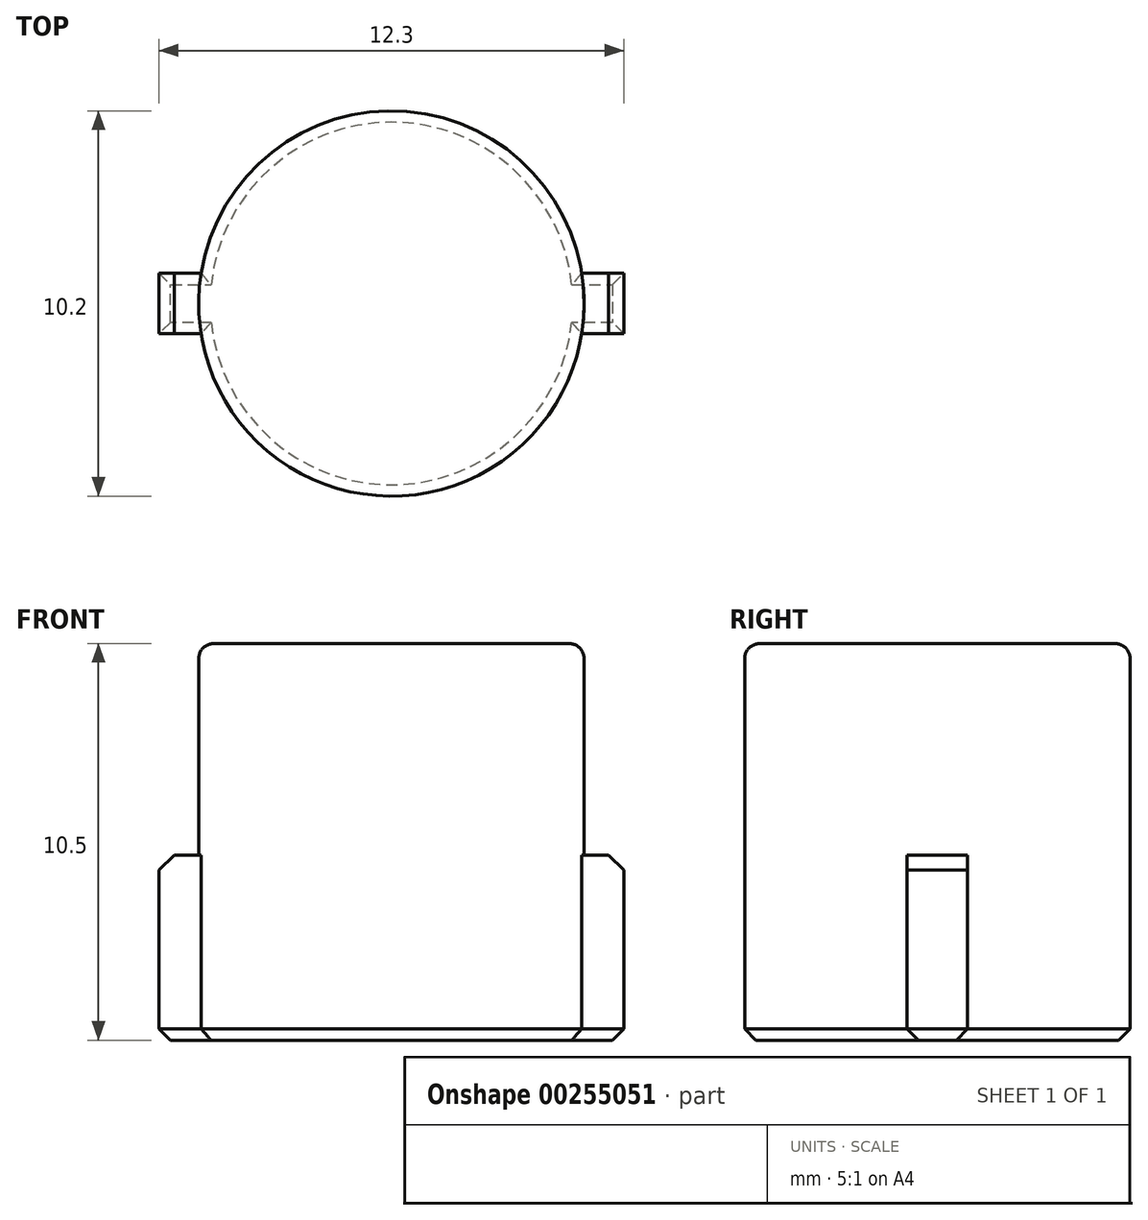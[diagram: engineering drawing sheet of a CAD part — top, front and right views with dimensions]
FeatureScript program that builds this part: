
annotation { "Feature Type Name" : "Feature", "Feature Type Description" : "" }
export const myFeature = defineFeature(function(context is Context, id is Id, definition is map)
    precondition{}
    {
        {
            var Q0;
            Q0=qCreatedBy(makeId("Top.planeOp"),FACE);
            var sketch = newSketch(context, id + "F0", { "sketchPlane" : qUnion([Q0])});
            skCircle(sketch, "E0", {"center": v(0, 0) * mm, "radius": 5.1 * mm});
            skSolve(sketch);
        }
        {
            var Q0;
            Q0=qSketchRegion(id+"F0",true);
            extrude(context, id + "F1", {"entities" : qUnion([Q0]), "depth" : 12.8 * mm});
        }
        {
            var Q0;
            Q0=makeQuery(id+"F1.opExtrude","CAP_FACE",FACE,{"disambiguationData":[OSD([sQuery(id+"F0.wireOp",EDGE,"E0")])],"isStart":true});
            var sketch = newSketch(context, id + "F2", { "sketchPlane" : qUnion([Q0])});
            skLineSegment(sketch, "E1.bottom", {"start": v(6.15, 0.8) * mm, "end": v(-6.15, 0.8) * mm});
            skLineSegment(sketch, "E1.top", {"start": v(6.15, -0.8) * mm, "end": v(-6.15, -0.8) * mm});
            skLineSegment(sketch, "E1.left", {"start": v(6.15, 0.8) * mm, "end": v(6.15, -0.8) * mm});
            skLineSegment(sketch, "E1.right", {"start": v(-6.15, 0.8) * mm, "end": v(-6.15, -0.8) * mm});
            skPoint(sketch, "E1.middle", {"position": v(0, 0) * mm});
            skCircle(sketch, "E2", {"center": v(0, 0) * mm, "radius": 6.2 * mm});
            skLineSegment(sketch, "E3.1.0", {"start": v(5.72, 2.38) * mm, "end": v(-4.92, -3.77) * mm});
            skLineSegment(sketch, "E3.1.1", {"start": v(4.92, 3.77) * mm, "end": v(-5.72, -2.38) * mm});
            skLineSegment(sketch, "E3.2.0", {"start": v(3.77, 4.92) * mm, "end": v(-2.38, -5.72) * mm});
            skLineSegment(sketch, "E3.2.1", {"start": v(2.38, 5.72) * mm, "end": v(-3.77, -4.92) * mm});
            skLineSegment(sketch, "E3.3.0", {"start": v(0.8, 6.15) * mm, "end": v(0.8, -6.15) * mm});
            skLineSegment(sketch, "E3.3.1", {"start": v(-0.8, 6.15) * mm, "end": v(-0.8, -6.15) * mm});
            skLineSegment(sketch, "E3.4.0", {"start": v(-2.38, 5.72) * mm, "end": v(3.77, -4.92) * mm});
            skLineSegment(sketch, "E3.4.1", {"start": v(-3.77, 4.92) * mm, "end": v(2.38, -5.72) * mm});
            skLineSegment(sketch, "E3.5.0", {"start": v(-4.92, 3.77) * mm, "end": v(5.72, -2.38) * mm});
            skLineSegment(sketch, "E3.5.1", {"start": v(-5.72, 2.38) * mm, "end": v(4.92, -3.77) * mm});
            skLineSegment(sketch, "E3.6.0", {"start": v(-6.15, 0.8) * mm, "end": v(6.15, 0.8) * mm});
            skLineSegment(sketch, "E3.6.1", {"start": v(-6.15, -0.8) * mm, "end": v(6.15, -0.8) * mm});
            skLineSegment(sketch, "E3.7.0", {"start": v(-5.72, -2.38) * mm, "end": v(4.92, 3.77) * mm});
            skLineSegment(sketch, "E3.7.1", {"start": v(-4.92, -3.77) * mm, "end": v(5.72, 2.38) * mm});
            skLineSegment(sketch, "E3.8.0", {"start": v(-3.77, -4.92) * mm, "end": v(2.38, 5.72) * mm});
            skLineSegment(sketch, "E3.8.1", {"start": v(-2.38, -5.72) * mm, "end": v(3.77, 4.92) * mm});
            skLineSegment(sketch, "E3.9.0", {"start": v(-0.8, -6.15) * mm, "end": v(-0.8, 6.15) * mm});
            skLineSegment(sketch, "E3.9.1", {"start": v(0.8, -6.15) * mm, "end": v(0.8, 6.15) * mm});
            skLineSegment(sketch, "E3.10.0", {"start": v(2.38, -5.72) * mm, "end": v(-3.77, 4.92) * mm});
            skLineSegment(sketch, "E3.10.1", {"start": v(3.77, -4.92) * mm, "end": v(-2.38, 5.72) * mm});
            skLineSegment(sketch, "E3.11.0", {"start": v(4.92, -3.77) * mm, "end": v(-5.72, 2.38) * mm});
            skLineSegment(sketch, "E3.11.1", {"start": v(5.72, -2.38) * mm, "end": v(-4.92, 3.77) * mm});
            skSolve(sketch);
        }
        {
            var Q0;
            {var subQ0=sQuery(id+"F2.wireOp",EDGE,"E3.8.0");var subQ1=sQuery(id+"F2.wireOp",EDGE,"E2");var subQ2=makeQuery(id+"F2.imprint","INTERSECT",VERTEX,{"disambiguationData":[OD(1.0)],"derivedFrom":[subQ1,subQ0]});Q0=makeQuery(id+"F2.imprint","IMPRINT",FACE,{"disambiguationData":[TD([[makeQuery(id+"F2.imprint","IMPRINT",EDGE,{"disambiguationData":[TD([[subQ2,1.0]])],"derivedFrom":subQ1}),1.0]])]});}
            var Q1;
            {var subQ0=sQuery(id+"F2.wireOp",EDGE,"E3.7.0");var subQ1=sQuery(id+"F2.wireOp",EDGE,"E2");var subQ2=makeQuery(id+"F2.imprint","INTERSECT",VERTEX,{"disambiguationData":[OD(1.0)],"derivedFrom":[subQ1,subQ0]});Q1=makeQuery(id+"F2.imprint","IMPRINT",FACE,{"disambiguationData":[TD([[makeQuery(id+"F2.imprint","IMPRINT",EDGE,{"disambiguationData":[TD([[subQ2,1.0]])],"derivedFrom":subQ1}),1.0]])]});}
            var Q2;
            {var subQ0=sQuery(id+"F2.wireOp",EDGE,"E1.left");Q2=makeQuery(id+"F2.imprint","IMPRINT",FACE,{"disambiguationData":[TD([[makeQuery(id+"F2.imprint","IMPRINT",EDGE,{"derivedFrom":subQ0}),-1.0]])]});}
            var Q3;
            {var subQ0=sQuery(id+"F2.wireOp",EDGE,"E3.11.0");var subQ1=sQuery(id+"F2.wireOp",EDGE,"E2");var subQ2=makeQuery(id+"F2.imprint","INTERSECT",VERTEX,{"disambiguationData":[OD(0.0)],"derivedFrom":[subQ1,subQ0]});Q3=makeQuery(id+"F2.imprint","IMPRINT",FACE,{"disambiguationData":[TD([[makeQuery(id+"F2.imprint","IMPRINT",EDGE,{"disambiguationData":[TD([[subQ2,-1.0]])],"derivedFrom":subQ1}),1.0]])]});}
            var Q4;
            {var subQ0=sQuery(id+"F2.wireOp",EDGE,"E3.10.0");var subQ1=sQuery(id+"F2.wireOp",EDGE,"E2");var subQ2=makeQuery(id+"F2.imprint","INTERSECT",VERTEX,{"disambiguationData":[OD(0.0)],"derivedFrom":[subQ1,subQ0]});Q4=makeQuery(id+"F2.imprint","IMPRINT",FACE,{"disambiguationData":[TD([[makeQuery(id+"F2.imprint","IMPRINT",EDGE,{"disambiguationData":[TD([[subQ2,-1.0]])],"derivedFrom":subQ1}),1.0]])]});}
            var Q5;
            {var subQ0=sQuery(id+"F2.wireOp",EDGE,"E3.8.0");var subQ1=sQuery(id+"F2.wireOp",EDGE,"E2");var subQ2=makeQuery(id+"F2.imprint","INTERSECT",VERTEX,{"disambiguationData":[OD(0.0)],"derivedFrom":[subQ1,subQ0]});Q5=makeQuery(id+"F2.imprint","IMPRINT",FACE,{"disambiguationData":[TD([[makeQuery(id+"F2.imprint","IMPRINT",EDGE,{"disambiguationData":[TD([[subQ2,-1.0]])],"derivedFrom":subQ1}),1.0]])]});}
            var Q6;
            {var subQ0=sQuery(id+"F2.wireOp",EDGE,"E3.9.0");var subQ1=sQuery(id+"F2.wireOp",EDGE,"E2");var subQ2=makeQuery(id+"F2.imprint","INTERSECT",VERTEX,{"disambiguationData":[OD(0.0)],"derivedFrom":[subQ1,subQ0]});Q6=makeQuery(id+"F2.imprint","IMPRINT",FACE,{"disambiguationData":[TD([[makeQuery(id+"F2.imprint","IMPRINT",EDGE,{"disambiguationData":[TD([[subQ2,-1.0]])],"derivedFrom":subQ1}),1.0]])]});}
            var Q7;
            {var subQ0=sQuery(id+"F2.wireOp",EDGE,"E3.7.0");var subQ1=sQuery(id+"F2.wireOp",EDGE,"E2");var subQ2=makeQuery(id+"F2.imprint","INTERSECT",VERTEX,{"disambiguationData":[OD(0.0)],"derivedFrom":[subQ1,subQ0]});Q7=makeQuery(id+"F2.imprint","IMPRINT",FACE,{"disambiguationData":[TD([[makeQuery(id+"F2.imprint","IMPRINT",EDGE,{"disambiguationData":[TD([[subQ2,-1.0]])],"derivedFrom":subQ1}),1.0]])]});}
            var Q8;
            {var subQ0=sQuery(id+"F2.wireOp",EDGE,"E1.right");Q8=makeQuery(id+"F2.imprint","IMPRINT",FACE,{"disambiguationData":[TD([[makeQuery(id+"F2.imprint","IMPRINT",EDGE,{"derivedFrom":subQ0}),1.0]])]});}
            var Q9;
            {var subQ0=sQuery(id+"F2.wireOp",EDGE,"E3.11.0");var subQ1=sQuery(id+"F2.wireOp",EDGE,"E2");var subQ2=makeQuery(id+"F2.imprint","INTERSECT",VERTEX,{"disambiguationData":[OD(1.0)],"derivedFrom":[subQ1,subQ0]});Q9=makeQuery(id+"F2.imprint","IMPRINT",FACE,{"disambiguationData":[TD([[makeQuery(id+"F2.imprint","IMPRINT",EDGE,{"disambiguationData":[TD([[subQ2,1.0]])],"derivedFrom":subQ1}),1.0]])]});}
            var Q10;
            {var subQ0=sQuery(id+"F2.wireOp",EDGE,"E3.10.0");var subQ1=sQuery(id+"F2.wireOp",EDGE,"E2");var subQ2=makeQuery(id+"F2.imprint","INTERSECT",VERTEX,{"disambiguationData":[OD(1.0)],"derivedFrom":[subQ1,subQ0]});Q10=makeQuery(id+"F2.imprint","IMPRINT",FACE,{"disambiguationData":[TD([[makeQuery(id+"F2.imprint","IMPRINT",EDGE,{"disambiguationData":[TD([[subQ2,1.0]])],"derivedFrom":subQ1}),1.0]])]});}
            var Q11;
            {var subQ0=sQuery(id+"F2.wireOp",EDGE,"E3.9.0");var subQ1=sQuery(id+"F2.wireOp",EDGE,"E2");var subQ2=makeQuery(id+"F2.imprint","INTERSECT",VERTEX,{"disambiguationData":[OD(1.0)],"derivedFrom":[subQ1,subQ0]});Q11=makeQuery(id+"F2.imprint","IMPRINT",FACE,{"disambiguationData":[TD([[makeQuery(id+"F2.imprint","IMPRINT",EDGE,{"disambiguationData":[TD([[subQ2,1.0]])],"derivedFrom":subQ1}),1.0]])]});}
            extrude(context, id + "F3", {"entities" : qUnion([Q0, Q1, Q2, Q3, Q4, Q5, Q6, Q7, Q8, Q9, Q10, Q11]), "operationType" : NewBodyOperationType.ADD, "oppositeDirection" : true, "depth" : 7.2 * mm});
        }
        {
            var Q0;
            {var subQ0=sQuery(id+"F2.wireOp",EDGE,"E2");Q0=makeQuery(id+"F3.opExtrude","CAP_EDGE",EDGE,{"disambiguationData":[OSD([subQ0]),TDD([makeQuery(id+"F2.imprint","IMPRINT",EDGE,{"disambiguationData":[TD([[makeQuery(id+"F2.imprint","INTERSECT",VERTEX,{"disambiguationData":[OD(1.0)],"derivedFrom":[subQ0,sQuery(id+"F2.wireOp",EDGE,"E3.9.0")]}),1.0]])],"derivedFrom":subQ0})])],"isStart":false});}
            var Q1;
            {var subQ0=sQuery(id+"F2.wireOp",EDGE,"E2");Q1=makeQuery(id+"F3.opExtrude","CAP_EDGE",EDGE,{"disambiguationData":[OSD([subQ0]),TDD([makeQuery(id+"F2.imprint","IMPRINT",EDGE,{"disambiguationData":[TD([[makeQuery(id+"F2.imprint","INTERSECT",VERTEX,{"disambiguationData":[OD(1.0)],"derivedFrom":[subQ0,sQuery(id+"F2.wireOp",EDGE,"E3.10.0")]}),1.0]])],"derivedFrom":subQ0})])],"isStart":false});}
            var Q2;
            {var subQ0=sQuery(id+"F2.wireOp",EDGE,"E2");Q2=makeQuery(id+"F3.opExtrude","CAP_EDGE",EDGE,{"disambiguationData":[OSD([subQ0]),TDD([makeQuery(id+"F2.imprint","IMPRINT",EDGE,{"disambiguationData":[TD([[makeQuery(id+"F2.imprint","INTERSECT",VERTEX,{"disambiguationData":[OD(1.0)],"derivedFrom":[subQ0,sQuery(id+"F2.wireOp",EDGE,"E3.11.0")]}),1.0]])],"derivedFrom":subQ0})])],"isStart":false});}
            var Q3;
            Q3=makeQuery(id+"F3.opExtrude","CAP_EDGE",EDGE,{"disambiguationData":[OSD([sQuery(id+"F2.wireOp",EDGE,"E1.right")])],"isStart":false});
            var Q4;
            {var subQ0=sQuery(id+"F2.wireOp",EDGE,"E2");Q4=makeQuery(id+"F3.opExtrude","CAP_EDGE",EDGE,{"disambiguationData":[OSD([subQ0]),TDD([makeQuery(id+"F2.imprint","IMPRINT",EDGE,{"disambiguationData":[TD([[makeQuery(id+"F2.imprint","INTERSECT",VERTEX,{"disambiguationData":[OD(1.0)],"derivedFrom":[subQ0,sQuery(id+"F2.wireOp",EDGE,"E3.8.0")]}),1.0]])],"derivedFrom":subQ0})])],"isStart":false});}
            var Q5;
            {var subQ0=sQuery(id+"F2.wireOp",EDGE,"E2");Q5=makeQuery(id+"F3.opExtrude","CAP_EDGE",EDGE,{"disambiguationData":[OSD([subQ0]),TDD([makeQuery(id+"F2.imprint","IMPRINT",EDGE,{"disambiguationData":[TD([[makeQuery(id+"F2.imprint","INTERSECT",VERTEX,{"disambiguationData":[OD(1.0)],"derivedFrom":[subQ0,sQuery(id+"F2.wireOp",EDGE,"E3.7.0")]}),1.0]])],"derivedFrom":subQ0})])],"isStart":false});}
            var Q6;
            Q6=makeQuery(id+"F3.opExtrude","CAP_EDGE",EDGE,{"disambiguationData":[OSD([sQuery(id+"F2.wireOp",EDGE,"E1.left")])],"isStart":false});
            var Q7;
            {var subQ0=sQuery(id+"F2.wireOp",EDGE,"E2");Q7=makeQuery(id+"F3.opExtrude","CAP_EDGE",EDGE,{"disambiguationData":[OSD([subQ0]),TDD([makeQuery(id+"F2.imprint","IMPRINT",EDGE,{"disambiguationData":[TD([[makeQuery(id+"F2.imprint","INTERSECT",VERTEX,{"disambiguationData":[OD(0.0)],"derivedFrom":[subQ0,sQuery(id+"F2.wireOp",EDGE,"E3.11.0")]}),-1.0]])],"derivedFrom":subQ0})])],"isStart":false});}
            var Q8;
            {var subQ0=sQuery(id+"F2.wireOp",EDGE,"E2");Q8=makeQuery(id+"F3.opExtrude","CAP_EDGE",EDGE,{"disambiguationData":[OSD([subQ0]),TDD([makeQuery(id+"F2.imprint","IMPRINT",EDGE,{"disambiguationData":[TD([[makeQuery(id+"F2.imprint","INTERSECT",VERTEX,{"disambiguationData":[OD(0.0)],"derivedFrom":[subQ0,sQuery(id+"F2.wireOp",EDGE,"E3.10.0")]}),-1.0]])],"derivedFrom":subQ0})])],"isStart":false});}
            var Q9;
            {var subQ0=sQuery(id+"F2.wireOp",EDGE,"E2");Q9=makeQuery(id+"F3.opExtrude","CAP_EDGE",EDGE,{"disambiguationData":[OSD([subQ0]),TDD([makeQuery(id+"F2.imprint","IMPRINT",EDGE,{"disambiguationData":[TD([[makeQuery(id+"F2.imprint","INTERSECT",VERTEX,{"disambiguationData":[OD(0.0)],"derivedFrom":[subQ0,sQuery(id+"F2.wireOp",EDGE,"E3.9.0")]}),-1.0]])],"derivedFrom":subQ0})])],"isStart":false});}
            var Q10;
            {var subQ0=sQuery(id+"F2.wireOp",EDGE,"E2");Q10=makeQuery(id+"F3.opExtrude","CAP_EDGE",EDGE,{"disambiguationData":[OSD([subQ0]),TDD([makeQuery(id+"F2.imprint","IMPRINT",EDGE,{"disambiguationData":[TD([[makeQuery(id+"F2.imprint","INTERSECT",VERTEX,{"disambiguationData":[OD(0.0)],"derivedFrom":[subQ0,sQuery(id+"F2.wireOp",EDGE,"E3.8.0")]}),-1.0]])],"derivedFrom":subQ0})])],"isStart":false});}
            var Q11;
            {var subQ0=sQuery(id+"F2.wireOp",EDGE,"E2");Q11=makeQuery(id+"F3.opExtrude","CAP_EDGE",EDGE,{"disambiguationData":[OSD([subQ0]),TDD([makeQuery(id+"F2.imprint","IMPRINT",EDGE,{"disambiguationData":[TD([[makeQuery(id+"F2.imprint","INTERSECT",VERTEX,{"disambiguationData":[OD(0.0)],"derivedFrom":[subQ0,sQuery(id+"F2.wireOp",EDGE,"E3.7.0")]}),-1.0]])],"derivedFrom":subQ0})])],"isStart":false});}
            chamfer(context, id + "F4", {"entities" : qUnion([Q0, Q1, Q2, Q3, Q4, Q5, Q6, Q7, Q8, Q9, Q10, Q11]), "width" : 0.4 * mm, "tangentPropagation" : true});
        }
        {
            var Q0;
            {var subQ0=sQuery(id+"F2.wireOp",EDGE,"E3.11.0");var subQ1=sQuery(id+"F0.wireOp",EDGE,"E0");var subQ2=makeQuery(id+"F1.opExtrude","CAP_EDGE",EDGE,{"disambiguationData":[OSD([subQ1])],"isStart":true});var subQ3=makeQuery(id+"F2.imprint","INTERSECT",VERTEX,{"disambiguationData":[OD(0.0)],"derivedFrom":[subQ2,subQ0]});var subQ4=sQuery(id+"F2.wireOp",EDGE,"E3.11.1");var subQ6=sQuery(id+"F2.wireOp",EDGE,"E2");var subQ7=makeQuery(id+"F2.imprint","INTERSECT",VERTEX,{"disambiguationData":[OD(0.0)],"derivedFrom":[subQ6,subQ4]});var subQ8=makeQuery(id+"F2.imprint","INTERSECT",VERTEX,{"disambiguationData":[OD(0.0)],"derivedFrom":[subQ6,subQ0]});var subQ9=sQuery(id+"F2.wireOp",EDGE,"E3.10.0");var subQ10=makeQuery(id+"F2.imprint","INTERSECT",VERTEX,{"disambiguationData":[OD(0.0)],"derivedFrom":[subQ2,subQ9]});var subQ11=sQuery(id+"F2.wireOp",EDGE,"E3.10.1");var subQ13=makeQuery(id+"F2.imprint","INTERSECT",VERTEX,{"disambiguationData":[OD(0.0)],"derivedFrom":[subQ6,subQ11]});var subQ14=makeQuery(id+"F2.imprint","INTERSECT",VERTEX,{"disambiguationData":[OD(0.0)],"derivedFrom":[subQ6,subQ9]});var subQ15=sQuery(id+"F2.wireOp",EDGE,"E3.9.0");var subQ16=makeQuery(id+"F2.imprint","INTERSECT",VERTEX,{"disambiguationData":[OD(0.0)],"derivedFrom":[subQ2,subQ15]});var subQ17=sQuery(id+"F2.wireOp",EDGE,"E3.9.1");var subQ19=makeQuery(id+"F2.imprint","INTERSECT",VERTEX,{"disambiguationData":[OD(0.0)],"derivedFrom":[subQ6,subQ17]});var subQ20=makeQuery(id+"F2.imprint","INTERSECT",VERTEX,{"disambiguationData":[OD(0.0)],"derivedFrom":[subQ6,subQ15]});var subQ21=sQuery(id+"F2.wireOp",EDGE,"E3.8.0");var subQ22=makeQuery(id+"F2.imprint","INTERSECT",VERTEX,{"disambiguationData":[OD(0.0)],"derivedFrom":[subQ2,subQ21]});var subQ23=sQuery(id+"F2.wireOp",EDGE,"E3.8.1");var subQ25=makeQuery(id+"F2.imprint","INTERSECT",VERTEX,{"disambiguationData":[OD(0.0)],"derivedFrom":[subQ6,subQ23]});var subQ26=makeQuery(id+"F2.imprint","INTERSECT",VERTEX,{"disambiguationData":[OD(0.0)],"derivedFrom":[subQ6,subQ21]});var subQ27=sQuery(id+"F2.wireOp",EDGE,"E3.7.0");var subQ28=makeQuery(id+"F2.imprint","INTERSECT",VERTEX,{"disambiguationData":[OD(0.0)],"derivedFrom":[subQ2,subQ27]});var subQ29=sQuery(id+"F2.wireOp",EDGE,"E3.7.1");var subQ31=makeQuery(id+"F2.imprint","INTERSECT",VERTEX,{"disambiguationData":[OD(0.0)],"derivedFrom":[subQ6,subQ29]});var subQ32=makeQuery(id+"F2.imprint","INTERSECT",VERTEX,{"disambiguationData":[OD(0.0)],"derivedFrom":[subQ6,subQ27]});var subQ33=makeQuery(id+"F2.imprint","INTERSECT",VERTEX,{"disambiguationData":[OD(1.0)],"derivedFrom":[subQ2,subQ0]});var subQ35=makeQuery(id+"F2.imprint","INTERSECT",VERTEX,{"disambiguationData":[OD(1.0)],"derivedFrom":[subQ6,subQ4]});var subQ36=makeQuery(id+"F2.imprint","INTERSECT",VERTEX,{"disambiguationData":[OD(1.0)],"derivedFrom":[subQ6,subQ0]});var subQ37=makeQuery(id+"F2.imprint","INTERSECT",VERTEX,{"disambiguationData":[OD(1.0)],"derivedFrom":[subQ2,subQ9]});var subQ39=makeQuery(id+"F2.imprint","INTERSECT",VERTEX,{"disambiguationData":[OD(1.0)],"derivedFrom":[subQ6,subQ11]});var subQ40=makeQuery(id+"F2.imprint","INTERSECT",VERTEX,{"disambiguationData":[OD(1.0)],"derivedFrom":[subQ6,subQ9]});var subQ41=makeQuery(id+"F2.imprint","INTERSECT",VERTEX,{"disambiguationData":[OD(1.0)],"derivedFrom":[subQ2,subQ15]});var subQ43=makeQuery(id+"F2.imprint","INTERSECT",VERTEX,{"disambiguationData":[OD(1.0)],"derivedFrom":[subQ6,subQ17]});var subQ44=makeQuery(id+"F2.imprint","INTERSECT",VERTEX,{"disambiguationData":[OD(1.0)],"derivedFrom":[subQ6,subQ15]});var subQ45=makeQuery(id+"F2.imprint","INTERSECT",VERTEX,{"disambiguationData":[OD(1.0)],"derivedFrom":[subQ2,subQ21]});var subQ47=makeQuery(id+"F2.imprint","INTERSECT",VERTEX,{"disambiguationData":[OD(1.0)],"derivedFrom":[subQ6,subQ23]});var subQ48=makeQuery(id+"F2.imprint","INTERSECT",VERTEX,{"disambiguationData":[OD(1.0)],"derivedFrom":[subQ6,subQ21]});var subQ49=makeQuery(id+"F2.imprint","INTERSECT",VERTEX,{"disambiguationData":[OD(1.0)],"derivedFrom":[subQ2,subQ27]});var subQ51=makeQuery(id+"F2.imprint","INTERSECT",VERTEX,{"disambiguationData":[OD(1.0)],"derivedFrom":[subQ6,subQ29]});var subQ52=makeQuery(id+"F2.imprint","INTERSECT",VERTEX,{"disambiguationData":[OD(1.0)],"derivedFrom":[subQ6,subQ27]});var subQ53=sQuery(id+"F2.wireOp",EDGE,"E3.6.1");var subQ54=sQuery(id+"F2.wireOp",EDGE,"E3.6.0");Q0=makeQuery(id+"F3.boolean.opBoolean","MERGE",FACE,{"derivedFrom":[makeQuery(id+"F1.opExtrude","CAP_FACE",FACE,{"disambiguationData":[OSD([subQ1])],"isStart":true}),makeQuery(id+"F3.opExtrude","CAP_FACE",FACE,{"disambiguationData":[OSD([subQ1,sQuery(id+"F2.wireOp",EDGE,"E1.left"),subQ54,subQ53])],"isStart":true}),makeQuery(id+"F3.opExtrude","CAP_FACE",FACE,{"disambiguationData":[OSD([subQ1,sQuery(id+"F2.wireOp",EDGE,"E1.right"),subQ54,subQ53])],"isStart":true}),makeQuery(id+"F3.opExtrude","CAP_FACE",FACE,{"disambiguationData":[OSD([subQ1,subQ6,subQ27,subQ29]),TDD([makeQuery(id+"F2.imprint","IMPRINT",EDGE,{"disambiguationData":[TD([[subQ52,1.0]])],"derivedFrom":subQ6}),makeQuery(id+"F2.imprint","IMPRINT",EDGE,{"disambiguationData":[TD([[subQ52,1.0]])],"derivedFrom":subQ27}),makeQuery(id+"F2.imprint","IMPRINT",EDGE,{"disambiguationData":[TD([[subQ51,1.0]])],"derivedFrom":subQ29}),makeQuery(id+"F2.imprint","IMPRINT",EDGE,{"disambiguationData":[TD([[subQ49,-1.0]])],"derivedFrom":subQ2})])],"isStart":true}),makeQuery(id+"F3.opExtrude","CAP_FACE",FACE,{"disambiguationData":[OSD([subQ1,subQ6,subQ21,subQ23]),TDD([makeQuery(id+"F2.imprint","IMPRINT",EDGE,{"disambiguationData":[TD([[subQ48,1.0]])],"derivedFrom":subQ6}),makeQuery(id+"F2.imprint","IMPRINT",EDGE,{"disambiguationData":[TD([[subQ48,1.0]])],"derivedFrom":subQ21}),makeQuery(id+"F2.imprint","IMPRINT",EDGE,{"disambiguationData":[TD([[subQ47,1.0]])],"derivedFrom":subQ23}),makeQuery(id+"F2.imprint","IMPRINT",EDGE,{"disambiguationData":[TD([[subQ45,-1.0]])],"derivedFrom":subQ2})])],"isStart":true}),makeQuery(id+"F3.opExtrude","CAP_FACE",FACE,{"disambiguationData":[OSD([subQ1,subQ6,subQ15,subQ17]),TDD([makeQuery(id+"F2.imprint","IMPRINT",EDGE,{"disambiguationData":[TD([[subQ44,1.0]])],"derivedFrom":subQ6}),makeQuery(id+"F2.imprint","IMPRINT",EDGE,{"disambiguationData":[TD([[subQ44,1.0]])],"derivedFrom":subQ15}),makeQuery(id+"F2.imprint","IMPRINT",EDGE,{"disambiguationData":[TD([[subQ43,1.0]])],"derivedFrom":subQ17}),makeQuery(id+"F2.imprint","IMPRINT",EDGE,{"disambiguationData":[TD([[subQ41,-1.0]])],"derivedFrom":subQ2})])],"isStart":true}),makeQuery(id+"F3.opExtrude","CAP_FACE",FACE,{"disambiguationData":[OSD([subQ1,subQ6,subQ9,subQ11]),TDD([makeQuery(id+"F2.imprint","IMPRINT",EDGE,{"disambiguationData":[TD([[subQ40,1.0]])],"derivedFrom":subQ6}),makeQuery(id+"F2.imprint","IMPRINT",EDGE,{"disambiguationData":[TD([[subQ40,1.0]])],"derivedFrom":subQ9}),makeQuery(id+"F2.imprint","IMPRINT",EDGE,{"disambiguationData":[TD([[subQ39,1.0]])],"derivedFrom":subQ11}),makeQuery(id+"F2.imprint","IMPRINT",EDGE,{"disambiguationData":[TD([[subQ37,-1.0]])],"derivedFrom":subQ2})])],"isStart":true}),makeQuery(id+"F3.opExtrude","CAP_FACE",FACE,{"disambiguationData":[OSD([subQ1,subQ6,subQ0,subQ4]),TDD([makeQuery(id+"F2.imprint","IMPRINT",EDGE,{"disambiguationData":[TD([[subQ36,1.0]])],"derivedFrom":subQ6}),makeQuery(id+"F2.imprint","IMPRINT",EDGE,{"disambiguationData":[TD([[subQ36,1.0]])],"derivedFrom":subQ0}),makeQuery(id+"F2.imprint","IMPRINT",EDGE,{"disambiguationData":[TD([[subQ35,1.0]])],"derivedFrom":subQ4}),makeQuery(id+"F2.imprint","IMPRINT",EDGE,{"disambiguationData":[TD([[subQ33,-1.0]])],"derivedFrom":subQ2})])],"isStart":true}),makeQuery(id+"F3.opExtrude","CAP_FACE",FACE,{"disambiguationData":[OSD([subQ1,subQ6,subQ27,subQ29]),TDD([makeQuery(id+"F2.imprint","IMPRINT",EDGE,{"disambiguationData":[TD([[subQ32,-1.0]])],"derivedFrom":subQ6}),makeQuery(id+"F2.imprint","IMPRINT",EDGE,{"disambiguationData":[TD([[subQ32,-1.0]])],"derivedFrom":subQ27}),makeQuery(id+"F2.imprint","IMPRINT",EDGE,{"disambiguationData":[TD([[subQ31,-1.0]])],"derivedFrom":subQ29}),makeQuery(id+"F2.imprint","IMPRINT",EDGE,{"disambiguationData":[TD([[subQ28,1.0]])],"derivedFrom":subQ2})])],"isStart":true}),makeQuery(id+"F3.opExtrude","CAP_FACE",FACE,{"disambiguationData":[OSD([subQ1,subQ6,subQ21,subQ23]),TDD([makeQuery(id+"F2.imprint","IMPRINT",EDGE,{"disambiguationData":[TD([[subQ26,-1.0]])],"derivedFrom":subQ6}),makeQuery(id+"F2.imprint","IMPRINT",EDGE,{"disambiguationData":[TD([[subQ26,-1.0]])],"derivedFrom":subQ21}),makeQuery(id+"F2.imprint","IMPRINT",EDGE,{"disambiguationData":[TD([[subQ25,-1.0]])],"derivedFrom":subQ23}),makeQuery(id+"F2.imprint","IMPRINT",EDGE,{"disambiguationData":[TD([[subQ22,1.0]])],"derivedFrom":subQ2})])],"isStart":true}),makeQuery(id+"F3.opExtrude","CAP_FACE",FACE,{"disambiguationData":[OSD([subQ1,subQ6,subQ15,subQ17]),TDD([makeQuery(id+"F2.imprint","IMPRINT",EDGE,{"disambiguationData":[TD([[subQ20,-1.0]])],"derivedFrom":subQ6}),makeQuery(id+"F2.imprint","IMPRINT",EDGE,{"disambiguationData":[TD([[subQ20,-1.0]])],"derivedFrom":subQ15}),makeQuery(id+"F2.imprint","IMPRINT",EDGE,{"disambiguationData":[TD([[subQ19,-1.0]])],"derivedFrom":subQ17}),makeQuery(id+"F2.imprint","IMPRINT",EDGE,{"disambiguationData":[TD([[subQ16,1.0]])],"derivedFrom":subQ2})])],"isStart":true}),makeQuery(id+"F3.opExtrude","CAP_FACE",FACE,{"disambiguationData":[OSD([subQ1,subQ6,subQ9,subQ11]),TDD([makeQuery(id+"F2.imprint","IMPRINT",EDGE,{"disambiguationData":[TD([[subQ14,-1.0]])],"derivedFrom":subQ6}),makeQuery(id+"F2.imprint","IMPRINT",EDGE,{"disambiguationData":[TD([[subQ14,-1.0]])],"derivedFrom":subQ9}),makeQuery(id+"F2.imprint","IMPRINT",EDGE,{"disambiguationData":[TD([[subQ13,-1.0]])],"derivedFrom":subQ11}),makeQuery(id+"F2.imprint","IMPRINT",EDGE,{"disambiguationData":[TD([[subQ10,1.0]])],"derivedFrom":subQ2})])],"isStart":true}),makeQuery(id+"F3.opExtrude","CAP_FACE",FACE,{"disambiguationData":[OSD([subQ1,subQ6,subQ0,subQ4]),TDD([makeQuery(id+"F2.imprint","IMPRINT",EDGE,{"disambiguationData":[TD([[subQ8,-1.0]])],"derivedFrom":subQ6}),makeQuery(id+"F2.imprint","IMPRINT",EDGE,{"disambiguationData":[TD([[subQ8,-1.0]])],"derivedFrom":subQ0}),makeQuery(id+"F2.imprint","IMPRINT",EDGE,{"disambiguationData":[TD([[subQ7,-1.0]])],"derivedFrom":subQ4}),makeQuery(id+"F2.imprint","IMPRINT",EDGE,{"disambiguationData":[TD([[subQ3,1.0]])],"derivedFrom":subQ2})])],"isStart":true})]});}
            var sketch = newSketch(context, id + "F5", { "sketchPlane" : qUnion([Q0])});
            skCircle(sketch, "E4", {"center": v(0, 0) * mm, "radius": 11.02 * mm});
            skSolve(sketch);
        }
        {
            var Q0;
            Q0=qSketchRegion(id+"F5",true);
            extrude(context, id + "F6", {"entities" : qUnion([Q0]), "operationType" : NewBodyOperationType.REMOVE, "oppositeDirection" : true, "depth" : 2.3 * mm});
        }
        {
            var Q0;
            Q0=makeQuery(id+"F1.opExtrude","CAP_EDGE",EDGE,{"disambiguationData":[OSD([sQuery(id+"F0.wireOp",EDGE,"E0")])],"isStart":false});
            fillet(context, id + "F7", {"entities" : qUnion([Q0]), "radius" : 0.4 * mm, "tangentPropagation" : true, "allowEdgeOverflow" : false});
        }
        {
            var Q0;
            Q0=makeQuery(id+"F6.boolean.opBoolean","COPY",FACE,{"derivedFrom":makeQuery(id+"F6.opExtrude","CAP_FACE",FACE,{"disambiguationData":[OSD([sQuery(id+"F5.wireOp",EDGE,"E4")])],"isStart":false})});
            chamfer(context, id + "F8", {"entities" : qUnion([Q0]), "width" : 0.3 * mm, "tangentPropagation" : true});
        }
    });
